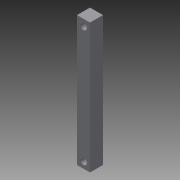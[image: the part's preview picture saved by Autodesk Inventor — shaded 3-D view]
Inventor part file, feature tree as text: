
AUTODESK INVENTOR PART (.ipt)
format: ipt  version: 2014 SP1 (Build 180222100, 222)  size: 79,360 bytes
history: native  units: in
note: dims shown in document units (in); Inventor stores cm internally (conversion verified against a paired STEP export)
features: sketch x2, extrude x1, hole x1
ambient origin geometry x8: Origin, YZ Plane, XZ Plane, XY Plane, X Axis, Y Axis, Z Axis, Center Point
bodies: Solid1 (feature_tree)
feature tree (4):
  extrude  "Extrusion1"  Depth=5.0in
  hole  "Hole1"  [1 undecoded]
  sketch  "Sketch1"  dims[d0=0.5in d1=5.0in]
  sketch  "Sketch2"  dims[d2=0.5in d3=0.0in d4=0.25in d5=0.25in d6=0.25in d7=0.75in d8=0.375in d9=0.25in d10=0.5635in d11=1.0in d12=0.8108in]
note: 1 required parameter value undecoded (feature->parameter linkage not recoverable at this tier; creation-order binding heuristic only, values carry confidence <= 0.55)
